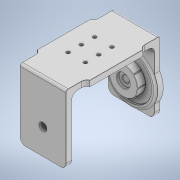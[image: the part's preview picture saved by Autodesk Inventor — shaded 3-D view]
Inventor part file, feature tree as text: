
AUTODESK INVENTOR PART (.ipt)
format: ipt  version: 2022 (Build 260153000, 153)  size: 628,736 bytes
history: native  units: mm
features: extrude x11, sketch x11, fillet x9, other x6, projected_geometry x2, mirror x1, pattern_circular x1, chamfer x1, revolve x1
ambient origin geometry x8: Origin, YZ Plane, XZ Plane, XY Plane, X Axis, Y Axis, Z Axis, Center Point
bodies: Body1 (feature_tree)
feature tree (43):
  other  "Твердое тело1"
  extrude  "Выдавливание1"  Depth=40.0mm
  extrude  "Выдавливание5"  Depth=81.5mm
  fillet  "Сопряжение3"  Radius=5.0mm
  other  "РабПлоскость1"
  extrude  "Выдавливание6"  Depth=45.8mm
  fillet  "Сопряжение4"  Radius=25.0mm
  fillet  "Сопряжение5"  Radius=3.0mm
  mirror  "Зеркальное отражение2"
  extrude  "Выдавливание7"  Depth=5.0mm
  other  "РабОсь6"
  extrude  "Выдавливание8"  Depth=55.0mm
  extrude  "Выдавливание9"  Depth=5.0mm TaperAngle=0.0deg
  extrude  "Выдавливание10"  Depth=5.0mm
  fillet  "Сопряжение7"  Radius=5.0mm
  other  "РабОсь1"
  pattern_circular  "Круговой массив1"  Count=4  [1 undecoded]
  fillet  "Сопряжение8"  Radius=7.0mm
  fillet  "Сопряжение11"  Radius=3.0mm
  other  "РабПлоскость3"
  extrude  "Выдавливание14"  Depth=37.8mm
  fillet  "Сопряжение13"  Radius=2.0mm
  fillet  "Сопряжение14"  Radius=1.4mm
  extrude  "Выдавливание16"  Depth=24.7mm
  extrude  "Выдавливание17"  Depth=6.9mm TaperAngle=0.0deg
  fillet  "Сопряжение16"  Radius=0.5mm
  extrude  "Выдавливание18"  Depth=1.4mm TaperAngle=0.0deg
  chamfer  "Фаска2"  Distance=0.4mm
  other  "РабПлоскость4"
  revolve  "Вращение1"
  sketch  "Эскиз1"
  sketch  "Эскиз5"
  sketch  "Эскиз6"
  sketch  "Эскиз7"
  projected_geometry  "Спроецированная петля1"
  sketch  "Эскиз9"
  sketch  "Эскиз10"
  sketch  "Эскиз17"
  sketch  "Эскиз19"
  sketch  "Эскиз20"
  projected_geometry  "Спроецированная петля3"
  sketch  "Эскиз21"
  sketch  "Эскиз22"
note: 1 required parameter value undecoded (feature->parameter linkage not recoverable at this tier; creation-order binding heuristic only, values carry confidence <= 0.55)
